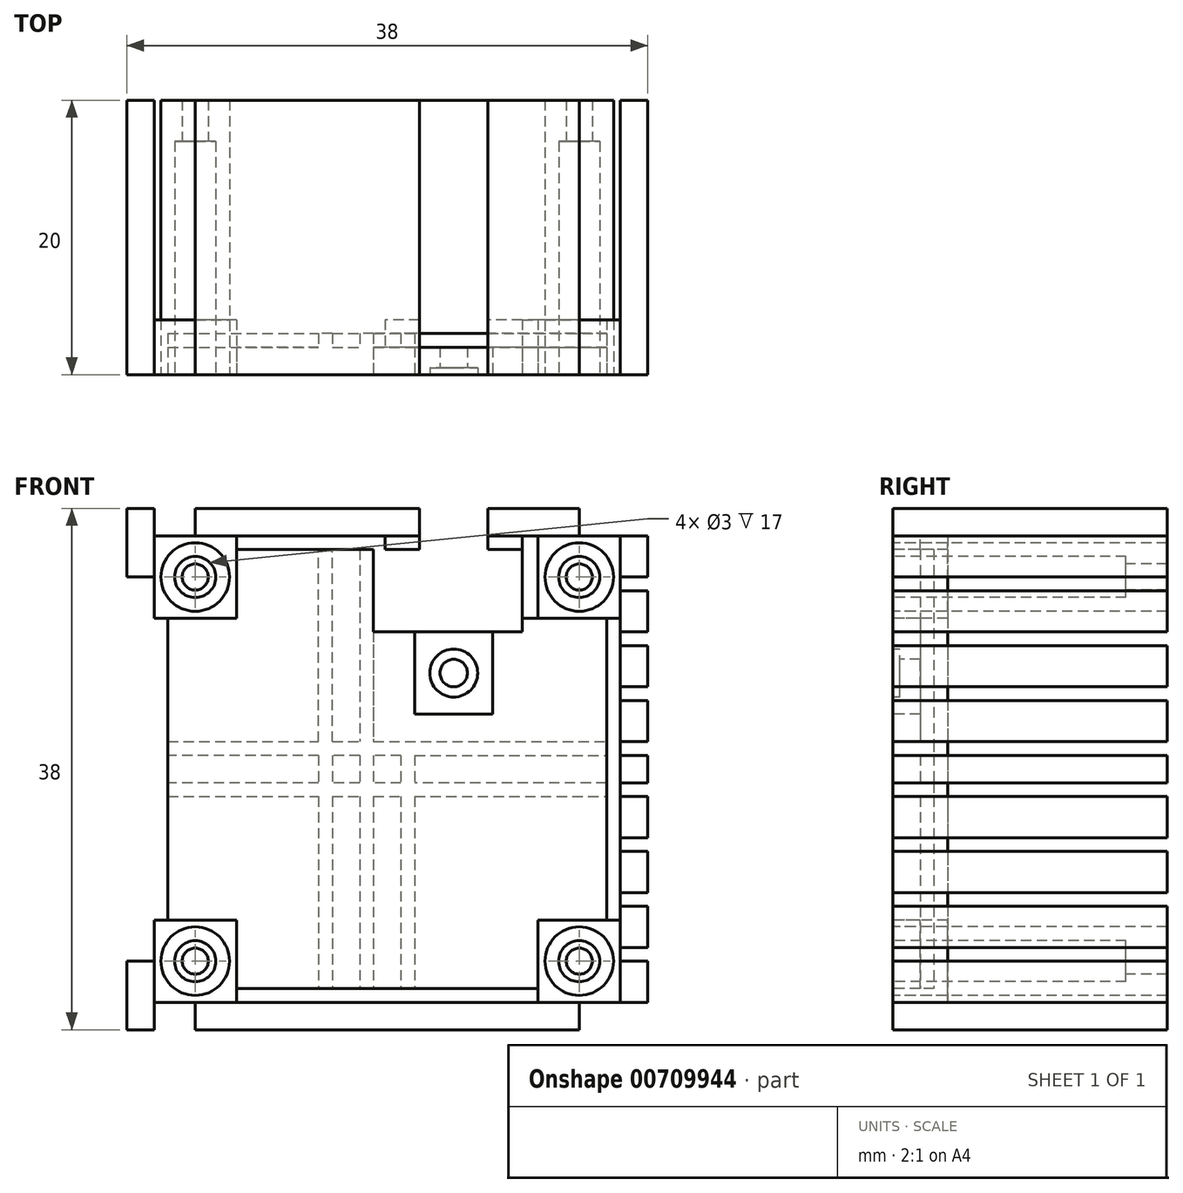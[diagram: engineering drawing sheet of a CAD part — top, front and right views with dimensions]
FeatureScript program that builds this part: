
annotation { "Feature Type Name" : "Feature", "Feature Type Description" : "" }
export const myFeature = defineFeature(function(context is Context, id is Id, definition is map)
    precondition{}
    {
        {
            var Q0;
            Q0=qCreatedBy(makeId("Front.planeOp"),FACE);
            var sketch = newSketch(context, id + "F0", { "sketchPlane" : qUnion([Q0])});
            skLineSegment(sketch, "E0.left", {"start": v(16, 10.17) * mm, "end": v(16, -11) * mm});
            skPoint(sketch, "E0.middle", {"position": v(0, 0) * mm});
            skCircle(sketch, "E1", {"center": v(-14, 14) * mm, "radius": 0.95 * mm});
            skCircle(sketch, "E2", {"center": v(14, -14) * mm, "radius": 0.95 * mm});
            skCircle(sketch, "E3", {"center": v(14, 14) * mm, "radius": 0.95 * mm});
            skCircle(sketch, "E4", {"center": v(-14, -14) * mm, "radius": 0.95 * mm});
            skPoint(sketch, "E5.left.start.orphan", {"position": v(10, -1.28) * mm});
            skPoint(sketch, "E6.trimOffspring.end.orphan", {"position": v(10, 1.28) * mm});
            skPoint(sketch, "E7.trimOffspring.end.orphan", {"position": v(-10, 1.28) * mm});
            skPoint(sketch, "E5.right.start.orphan", {"position": v(-10, -1.28) * mm});
            skLineSegment(sketch, "E8.left", {"start": v(16, 11) * mm, "end": v(16, 10.17) * mm});
            skLineSegment(sketch, "E8.right", {"start": v(9.85, 16) * mm, "end": v(9.85, 10.2) * mm});
            skLineSegment(sketch, "E9.bottom", {"start": v(9.85, 16) * mm, "end": v(-0.15, 16) * mm});
            skLineSegment(sketch, "E9.top", {"start": v(9.85, 10) * mm, "end": v(-0.15, 10) * mm});
            skLineSegment(sketch, "E9.left", {"start": v(9.85, 16) * mm, "end": v(9.85, 10) * mm});
            skLineSegment(sketch, "E9.right", {"start": v(-0.15, 16) * mm, "end": v(-0.15, 10) * mm});
            skLineSegment(sketch, "E10.top", {"start": v(-16, 10) * mm, "end": v(-10, 10) * mm});
            skLineSegment(sketch, "E11.top", {"start": v(-16, 4) * mm, "end": v(-10, 4) * mm});
            skLineSegment(sketch, "E11.left", {"start": v(-16, 10) * mm, "end": v(-16, 4) * mm});
            skLineSegment(sketch, "E11.right", {"start": v(-10, 10) * mm, "end": v(-10, 4) * mm});
            skLineSegment(sketch, "E12.bottom", {"start": v(17, 17) * mm, "end": v(-17, 17) * mm});
            skLineSegment(sketch, "E12.top", {"start": v(17, -17) * mm, "end": v(-17, -17) * mm});
            skLineSegment(sketch, "E12.left", {"start": v(17, 17) * mm, "end": v(17, -17) * mm});
            skLineSegment(sketch, "E12.right", {"start": v(-17, 17) * mm, "end": v(-17, -17) * mm});
            skLineSegment(sketch, "E13.bottom", {"start": v(19, 19) * mm, "end": v(-19, 19) * mm});
            skLineSegment(sketch, "E13.top", {"start": v(19, -19) * mm, "end": v(-19, -19) * mm});
            skLineSegment(sketch, "E13.left", {"start": v(19, 19) * mm, "end": v(19, -19) * mm});
            skLineSegment(sketch, "E13.right", {"start": v(-19, 19) * mm, "end": v(-19, -19) * mm});
            skCircle(sketch, "E14", {"center": v(-14, 14) * mm, "radius": 2.5 * mm});
            skCircle(sketch, "E15", {"center": v(14, 14) * mm, "radius": 2.5 * mm});
            skCircle(sketch, "E16", {"center": v(-14, -14) * mm, "radius": 2.5 * mm});
            skCircle(sketch, "E17", {"center": v(14, -14) * mm, "radius": 2.5 * mm});
            skLineSegment(sketch, "E18.trimOffspring", {"start": v(-16, 11) * mm, "end": v(-16, 10) * mm});
            skLineSegment(sketch, "E19.trimOffspring", {"start": v(-16, 11) * mm, "end": v(-16, -11) * mm});
            skPoint(sketch, "E20.trimOffspring.end.orphan", {"position": v(-16, 16) * mm});
            skLineSegment(sketch, "E21.trimOffspring", {"start": v(11, 16) * mm, "end": v(-11, 16) * mm});
            skLineSegment(sketch, "E22.trimOffspring", {"start": v(11, 16) * mm, "end": v(9.85, 16) * mm});
            skPoint(sketch, "E23.orphan", {"position": v(16, 15.97) * mm});
            skPoint(sketch, "E24.orphan", {"position": v(-16, -15.97) * mm});
            skLineSegment(sketch, "E25.trimOffspring", {"start": v(11, -16) * mm, "end": v(-11, -16) * mm});
            skPoint(sketch, "E26.trimOffspring.end.orphan", {"position": v(16, -16) * mm});
            skPoint(sketch, "E27", {"position": v(8.5, 2) * mm});
            skPoint(sketch, "E28", {"position": v(8.5, -2) * mm});
            skPoint(sketch, "E29", {"position": v(-8.5, 2) * mm});
            skPoint(sketch, "E30", {"position": v(-8.5, -2) * mm});
            skPoint(sketch, "E31.orphan", {"position": v(-8.5, 8.5) * mm});
            skPoint(sketch, "E32.right.start.orphan", {"position": v(-9.5, 9.5) * mm});
            skPoint(sketch, "E33.orphan", {"position": v(-8.5, -8.5) * mm});
            skPoint(sketch, "E32.left.start.orphan", {"position": v(9.5, 9.5) * mm});
            skPoint(sketch, "E34.orphan", {"position": v(8.5, 8.5) * mm});
            skPoint(sketch, "E32.top.end.orphan", {"position": v(-9.5, -9.5) * mm});
            skPoint(sketch, "E35.trimOffspring.end.orphan", {"position": v(9.5, -9.5) * mm});
            skPoint(sketch, "E36.orphan", {"position": v(8.5, -8.5) * mm});
            skLineSegment(sketch, "E37.bottom", {"start": v(2.35, 17) * mm, "end": v(7.35, 17) * mm});
            skLineSegment(sketch, "E37.left", {"start": v(2.35, 17) * mm, "end": v(2.35, 11) * mm});
            skLineSegment(sketch, "E37.right", {"start": v(7.35, 17) * mm, "end": v(7.35, 11) * mm});
            skPoint(sketch, "E37.middle", {"position": v(4.85, 13) * mm});
            skLineSegment(sketch, "E38", {"start": v(2.35, 17) * mm, "end": v(2.35, 19) * mm});
            skLineSegment(sketch, "E39", {"start": v(7.35, 17) * mm, "end": v(7.35, 19) * mm});
            skPoint(sketch, "E40.center.orphan", {"position": v(-10, 0) * mm});
            skPoint(sketch, "E41.center.orphan", {"position": v(10, 0) * mm});
            skPoint(sketch, "E42", {"position": v(7.35, 16) * mm});
            skLineSegment(sketch, "E43.bottom", {"start": v(2.35, 16) * mm, "end": v(7.35, 16) * mm});
            skLineSegment(sketch, "E43.top", {"start": v(2.35, 11) * mm, "end": v(7.35, 11) * mm});
            skLineSegment(sketch, "E43.left", {"start": v(2.35, 16) * mm, "end": v(2.35, 11) * mm});
            skLineSegment(sketch, "E43.right", {"start": v(7.35, 16) * mm, "end": v(7.35, 11) * mm});
            skPoint(sketch, "E44", {"position": v(2.35, 10) * mm});
            skPoint(sketch, "E45", {"position": v(7.35, 10) * mm});
            skPoint(sketch, "E37.top.start.orphan", {"position": v(2.35, 9) * mm});
            skPoint(sketch, "E46.orphan", {"position": v(7.35, 9) * mm});
            skPoint(sketch, "E47", {"position": v(2.35, 11) * mm});
            skPoint(sketch, "E48", {"position": v(7.35, 11) * mm});
            skLineSegment(sketch, "E49.bottom", {"start": v(-19, 19) * mm, "end": v(-17, 19) * mm});
            skLineSegment(sketch, "E49.top", {"start": v(-19, 17) * mm, "end": v(-17, 17) * mm});
            skLineSegment(sketch, "E49.left", {"start": v(-19, 19) * mm, "end": v(-19, 17) * mm});
            skLineSegment(sketch, "E49.right", {"start": v(-17, 19) * mm, "end": v(-17, 17) * mm});
            skLineSegment(sketch, "E50.bottom", {"start": v(19, 19) * mm, "end": v(17, 19) * mm});
            skLineSegment(sketch, "E50.top", {"start": v(19, 17) * mm, "end": v(17, 17) * mm});
            skLineSegment(sketch, "E50.left", {"start": v(19, 19) * mm, "end": v(19, 17) * mm});
            skLineSegment(sketch, "E50.right", {"start": v(17, 19) * mm, "end": v(17, 17) * mm});
            skLineSegment(sketch, "E51.bottom", {"start": v(17, -17) * mm, "end": v(19, -17) * mm});
            skLineSegment(sketch, "E51.top", {"start": v(17, -19) * mm, "end": v(19, -19) * mm});
            skLineSegment(sketch, "E51.left", {"start": v(17, -17) * mm, "end": v(17, -19) * mm});
            skLineSegment(sketch, "E51.right", {"start": v(19, -17) * mm, "end": v(19, -19) * mm});
            skLineSegment(sketch, "E52.bottom", {"start": v(-19, -19) * mm, "end": v(-17, -19) * mm});
            skLineSegment(sketch, "E52.top", {"start": v(-19, -17) * mm, "end": v(-17, -17) * mm});
            skLineSegment(sketch, "E52.left", {"start": v(-19, -19) * mm, "end": v(-19, -17) * mm});
            skLineSegment(sketch, "E52.right", {"start": v(-17, -19) * mm, "end": v(-17, -17) * mm});
            skLineSegment(sketch, "E53.bottom", {"start": v(-17, -17) * mm, "end": v(-19, -17) * mm});
            skLineSegment(sketch, "E53.top", {"start": v(-17, -14) * mm, "end": v(-19, -14) * mm});
            skLineSegment(sketch, "E53.left", {"start": v(-17, -17) * mm, "end": v(-17, -14) * mm});
            skLineSegment(sketch, "E53.right", {"start": v(-19, -17) * mm, "end": v(-19, -14) * mm});
            skLineSegment(sketch, "E54.top", {"start": v(17, -14) * mm, "end": v(19, -14) * mm});
            skLineSegment(sketch, "E54.left", {"start": v(17, -17) * mm, "end": v(17, -14) * mm});
            skLineSegment(sketch, "E54.right", {"start": v(19, -17) * mm, "end": v(19, -14) * mm});
            skLineSegment(sketch, "E55.bottom", {"start": v(-17, -17) * mm, "end": v(-14, -17) * mm});
            skLineSegment(sketch, "E55.top", {"start": v(-17, -19) * mm, "end": v(-14, -19) * mm});
            skLineSegment(sketch, "E55.left", {"start": v(-17, -17) * mm, "end": v(-17, -19) * mm});
            skLineSegment(sketch, "E55.right", {"start": v(-14, -17) * mm, "end": v(-14, -19) * mm});
            skLineSegment(sketch, "E56.bottom", {"start": v(17, -19) * mm, "end": v(14, -19) * mm});
            skLineSegment(sketch, "E56.top", {"start": v(17, -17) * mm, "end": v(14, -17) * mm});
            skLineSegment(sketch, "E56.left", {"start": v(17, -19) * mm, "end": v(17, -17) * mm});
            skLineSegment(sketch, "E56.right", {"start": v(14, -19) * mm, "end": v(14, -17) * mm});
            skLineSegment(sketch, "E57.top", {"start": v(-19, 14) * mm, "end": v(-17, 14) * mm});
            skLineSegment(sketch, "E57.left", {"start": v(-19, 17) * mm, "end": v(-19, 14) * mm});
            skLineSegment(sketch, "E57.right", {"start": v(-17, 17) * mm, "end": v(-17, 14) * mm});
            skLineSegment(sketch, "E58.bottom", {"start": v(-17, 19) * mm, "end": v(-14, 19) * mm});
            skLineSegment(sketch, "E58.top", {"start": v(-17, 17) * mm, "end": v(-14, 17) * mm});
            skLineSegment(sketch, "E58.right", {"start": v(-14, 19) * mm, "end": v(-14, 17) * mm});
            skLineSegment(sketch, "E59.bottom", {"start": v(17, 19) * mm, "end": v(14, 19) * mm});
            skLineSegment(sketch, "E59.top", {"start": v(17, 17) * mm, "end": v(14, 17) * mm});
            skLineSegment(sketch, "E59.right", {"start": v(14, 19) * mm, "end": v(14, 17) * mm});
            skLineSegment(sketch, "E60.top", {"start": v(19, 14) * mm, "end": v(17, 14) * mm});
            skLineSegment(sketch, "E60.left", {"start": v(19, 17) * mm, "end": v(19, 14) * mm});
            skLineSegment(sketch, "E60.right", {"start": v(17, 17) * mm, "end": v(17, 14) * mm});
            skLineSegment(sketch, "E61.bottom", {"start": v(17, 14) * mm, "end": v(19, 14) * mm});
            skLineSegment(sketch, "E61.top", {"start": v(17, 13) * mm, "end": v(19, 13) * mm});
            skLineSegment(sketch, "E61.left", {"start": v(17, 14) * mm, "end": v(17, 13) * mm});
            skLineSegment(sketch, "E61.right", {"start": v(19, 14) * mm, "end": v(19, 13) * mm});
            skPoint(sketch, "E62", {"position": v(19, 14) * mm});
            skPoint(sketch, "E63", {"position": v(19, 13) * mm});
            skLineSegment(sketch, "E64.top", {"start": v(17, 10) * mm, "end": v(19, 10) * mm});
            skLineSegment(sketch, "E64.left", {"start": v(17, 13) * mm, "end": v(17, 10) * mm});
            skLineSegment(sketch, "E64.right", {"start": v(19, 13) * mm, "end": v(19, 10) * mm});
            skLineSegment(sketch, "E65.top", {"start": v(17, 9) * mm, "end": v(19, 9) * mm});
            skLineSegment(sketch, "E65.left", {"start": v(17, 10) * mm, "end": v(17, 9) * mm});
            skLineSegment(sketch, "E65.right", {"start": v(19, 10) * mm, "end": v(19, 9) * mm});
            skLineSegment(sketch, "E66.top", {"start": v(17, 6) * mm, "end": v(19, 6) * mm});
            skLineSegment(sketch, "E66.left", {"start": v(17, 9) * mm, "end": v(17, 6) * mm});
            skLineSegment(sketch, "E66.right", {"start": v(19, 9) * mm, "end": v(19, 6) * mm});
            skLineSegment(sketch, "E67.top", {"start": v(17, 5) * mm, "end": v(19, 5) * mm});
            skLineSegment(sketch, "E67.left", {"start": v(17, 6) * mm, "end": v(17, 5) * mm});
            skLineSegment(sketch, "E67.right", {"start": v(19, 6) * mm, "end": v(19, 5) * mm});
            skLineSegment(sketch, "E68.top", {"start": v(17, 2) * mm, "end": v(19, 2) * mm});
            skLineSegment(sketch, "E68.left", {"start": v(17, 5) * mm, "end": v(17, 2) * mm});
            skLineSegment(sketch, "E68.right", {"start": v(19, 5) * mm, "end": v(19, 2) * mm});
            skLineSegment(sketch, "E69.left", {"start": v(17, 2) * mm, "end": v(17, 0) * mm});
            skLineSegment(sketch, "E69.right", {"start": v(19, 2) * mm, "end": v(19, 0) * mm});
            skLineSegment(sketch, "E70.top", {"start": v(17, -2) * mm, "end": v(19, -2) * mm});
            skLineSegment(sketch, "E70.left", {"start": v(17, 0) * mm, "end": v(17, -2) * mm});
            skLineSegment(sketch, "E70.right", {"start": v(19, 0) * mm, "end": v(19, -2) * mm});
            skLineSegment(sketch, "E71.top", {"start": v(17, -5) * mm, "end": v(19, -5) * mm});
            skLineSegment(sketch, "E71.left", {"start": v(17, -2) * mm, "end": v(17, -5) * mm});
            skLineSegment(sketch, "E71.right", {"start": v(19, -2) * mm, "end": v(19, -5) * mm});
            skLineSegment(sketch, "E72.top", {"start": v(17, -6) * mm, "end": v(19, -6) * mm});
            skLineSegment(sketch, "E72.left", {"start": v(17, -5) * mm, "end": v(17, -6) * mm});
            skLineSegment(sketch, "E72.right", {"start": v(19, -5) * mm, "end": v(19, -6) * mm});
            skLineSegment(sketch, "E73.top", {"start": v(17, -9) * mm, "end": v(19, -9) * mm});
            skLineSegment(sketch, "E73.left", {"start": v(17, -6) * mm, "end": v(17, -9) * mm});
            skLineSegment(sketch, "E73.right", {"start": v(19, -6) * mm, "end": v(19, -9) * mm});
            skLineSegment(sketch, "E74.top", {"start": v(17, -10) * mm, "end": v(19, -10) * mm});
            skLineSegment(sketch, "E74.left", {"start": v(17, -9) * mm, "end": v(17, -10) * mm});
            skLineSegment(sketch, "E74.right", {"start": v(19, -9) * mm, "end": v(19, -10) * mm});
            skLineSegment(sketch, "E75.top", {"start": v(17, -13) * mm, "end": v(19, -13) * mm});
            skLineSegment(sketch, "E75.left", {"start": v(17, -10) * mm, "end": v(17, -13) * mm});
            skLineSegment(sketch, "E75.right", {"start": v(19, -10) * mm, "end": v(19, -13) * mm});
            skLineSegment(sketch, "E76", {"start": v(17, -1) * mm, "end": v(19, -1) * mm});
            skLineSegment(sketch, "E77", {"start": v(17, 1) * mm, "end": v(19, 1) * mm});
            skLineSegment(sketch, "E78.bottom", {"start": v(1, 16) * mm, "end": v(-1, 16) * mm});
            skLineSegment(sketch, "E78.top", {"start": v(1, -16) * mm, "end": v(-1, -16) * mm});
            skLineSegment(sketch, "E78.right", {"start": v(-1, 16) * mm, "end": v(-1, 2) * mm});
            skLineSegment(sketch, "E79.top", {"start": v(16, -1) * mm, "end": v(2, -1) * mm});
            skLineSegment(sketch, "E79.left", {"start": v(17, 1) * mm, "end": v(17, -1) * mm});
            skLineSegment(sketch, "E79.right", {"start": v(-17, 1) * mm, "end": v(-17, -1) * mm});
            skLineSegment(sketch, "E80.bottom", {"start": v(-16, 2) * mm, "end": v(-5, 2) * mm});
            skLineSegment(sketch, "E80.top", {"start": v(-16, -2) * mm, "end": v(-5, -2) * mm});
            skLineSegment(sketch, "E80.left", {"start": v(-17, 2) * mm, "end": v(-17, -2) * mm});
            skLineSegment(sketch, "E80.right", {"start": v(17, 2) * mm, "end": v(17, -2) * mm});
            skLineSegment(sketch, "E81.bottom", {"start": v(-2, 16) * mm, "end": v(2, 16) * mm});
            skLineSegment(sketch, "E81.top", {"start": v(-2, -16) * mm, "end": v(2, -16) * mm});
            skLineSegment(sketch, "E81.left", {"start": v(-2, 16) * mm, "end": v(-2, 2) * mm});
            skLineSegment(sketch, "E81.right", {"start": v(2, 10) * mm, "end": v(2, 4) * mm});
            skLineSegment(sketch, "E82.trimOffspring", {"start": v(-1, 2) * mm, "end": v(1, 2) * mm});
            skLineSegment(sketch, "E83.trimOffspring", {"start": v(-2, 1) * mm, "end": v(-4, 1) * mm});
            skLineSegment(sketch, "E84.trimOffspring", {"start": v(2, 2) * mm, "end": v(16, 2) * mm});
            skLineSegment(sketch, "E85.trimOffspring", {"start": v(1, 1) * mm, "end": v(1, -1) * mm});
            skLineSegment(sketch, "E86.trimOffspring", {"start": v(1, 1) * mm, "end": v(-1, 1) * mm});
            skLineSegment(sketch, "E87.trimOffspring", {"start": v(1, -1) * mm, "end": v(-1, -1) * mm});
            skLineSegment(sketch, "E88.trimOffspring", {"start": v(2, -2) * mm, "end": v(16, -2) * mm});
            skPoint(sketch, "E89", {"position": v(2, -1) * mm});
            skPoint(sketch, "E90", {"position": v(2, -2) * mm});
            skPoint(sketch, "E91", {"position": v(1, -2) * mm});
            skPoint(sketch, "E92", {"position": v(1, -1) * mm});
            skPoint(sketch, "E93", {"position": v(-1, -1) * mm});
            skPoint(sketch, "E94", {"position": v(-1, -2) * mm});
            skPoint(sketch, "E95", {"position": v(-2, -2) * mm});
            skPoint(sketch, "E96", {"position": v(-2, -1) * mm});
            skPoint(sketch, "E97", {"position": v(-2, 1) * mm});
            skPoint(sketch, "E98", {"position": v(-1, 1) * mm});
            skLineSegment(sketch, "E99.trimOffspring", {"start": v(-2, -2) * mm, "end": v(-2, -16) * mm});
            skLineSegment(sketch, "E100.trimOffspring", {"start": v(-1, -2) * mm, "end": v(-1, -16) * mm});
            skLineSegment(sketch, "E101.trimOffspring", {"start": v(-1, -2) * mm, "end": v(1, -2) * mm});
            skLineSegment(sketch, "E102.trimOffspring", {"start": v(-2, 1) * mm, "end": v(-2, -1) * mm});
            skLineSegment(sketch, "E103.trimOffspring", {"start": v(-2, -1) * mm, "end": v(-4, -1) * mm});
            skLineSegment(sketch, "E104.trimOffspring", {"start": v(-1, 1) * mm, "end": v(-1, -1) * mm});
            skLineSegment(sketch, "E105.trimOffspring", {"start": v(2, 1) * mm, "end": v(2, -1) * mm});
            skLineSegment(sketch, "E106.trimOffspring", {"start": v(2, -2) * mm, "end": v(2, -16) * mm});
            skLineSegment(sketch, "E107.trimOffspring", {"start": v(1, -2) * mm, "end": v(1, -16) * mm});
            skLineSegment(sketch, "E108", {"start": v(2, 1) * mm, "end": v(16, 1) * mm});
            skCircle(sketch, "E109", {"center": v(14, 14) * mm, "radius": 1.5 * mm});
            skCircle(sketch, "E110", {"center": v(-14, 14) * mm, "radius": 1.5 * mm});
            skCircle(sketch, "E111", {"center": v(14, -14) * mm, "radius": 1.5 * mm});
            skCircle(sketch, "E112", {"center": v(-14, -14) * mm, "radius": 1.5 * mm});
            skLineSegment(sketch, "E113.bottom", {"start": v(17, 17) * mm, "end": v(11, 17) * mm});
            skLineSegment(sketch, "E113.top", {"start": v(17, 11) * mm, "end": v(11, 11) * mm});
            skLineSegment(sketch, "E113.left", {"start": v(17, 17) * mm, "end": v(17, 11) * mm});
            skLineSegment(sketch, "E113.right", {"start": v(11, 17) * mm, "end": v(11, 11) * mm});
            skLineSegment(sketch, "E114.bottom", {"start": v(-17, 17) * mm, "end": v(-11, 17) * mm});
            skLineSegment(sketch, "E114.top", {"start": v(-17, 11) * mm, "end": v(-11, 11) * mm});
            skLineSegment(sketch, "E114.left", {"start": v(-17, 17) * mm, "end": v(-17, 11) * mm});
            skLineSegment(sketch, "E114.right", {"start": v(-11, 17) * mm, "end": v(-11, 11) * mm});
            skLineSegment(sketch, "E115.bottom", {"start": v(-17, -17) * mm, "end": v(-11, -17) * mm});
            skLineSegment(sketch, "E115.top", {"start": v(-17, -11) * mm, "end": v(-11, -11) * mm});
            skLineSegment(sketch, "E115.left", {"start": v(-17, -17) * mm, "end": v(-17, -11) * mm});
            skLineSegment(sketch, "E115.right", {"start": v(-11, -17) * mm, "end": v(-11, -11) * mm});
            skLineSegment(sketch, "E116.bottom", {"start": v(17, -17) * mm, "end": v(11, -17) * mm});
            skLineSegment(sketch, "E116.top", {"start": v(17, -11) * mm, "end": v(11, -11) * mm});
            skLineSegment(sketch, "E116.left", {"start": v(17, -17) * mm, "end": v(17, -11) * mm});
            skLineSegment(sketch, "E116.right", {"start": v(11, -17) * mm, "end": v(11, -11) * mm});
            skLineSegment(sketch, "E117.bottom", {"start": v(9.85, 16) * mm, "end": v(11, 16) * mm});
            skLineSegment(sketch, "E117.top", {"start": v(9.85, 11) * mm, "end": v(11, 11) * mm});
            skLineSegment(sketch, "E117.left", {"start": v(9.85, 16) * mm, "end": v(9.85, 11) * mm});
            skLineSegment(sketch, "E117.right", {"start": v(11, 16) * mm, "end": v(11, 11) * mm});
            skLineSegment(sketch, "E118.bottom", {"start": v(-0.15, 16) * mm, "end": v(-1, 16) * mm});
            skLineSegment(sketch, "E118.top", {"start": v(-0.15, 10) * mm, "end": v(-1, 10) * mm});
            skLineSegment(sketch, "E118.right", {"start": v(-1, 16) * mm, "end": v(-1, 10) * mm});
            skPoint(sketch, "E119", {"position": v(4.85, 10) * mm});
            skArc(sketch, "E120", {"start": v(7.7, 7.94) * mm, "mid": v(4.85, 10) * mm, "end": v(2, 7.94) * mm});
            skCircle(sketch, "E121", {"center": v(4.85, 7) * mm, "radius": 1 * mm});
            skCircle(sketch, "E122", {"center": v(4.85, 7) * mm, "radius": 1.75 * mm});
            skLineSegment(sketch, "E123.bottom", {"start": v(2, 10) * mm, "end": v(7.7, 10) * mm});
            skLineSegment(sketch, "E123.top", {"start": v(2, 4) * mm, "end": v(7.7, 4) * mm});
            skLineSegment(sketch, "E123.right", {"start": v(7.7, 10) * mm, "end": v(7.7, 4) * mm});
            skArc(sketch, "E124.trimOffspring", {"start": v(2, 6.06) * mm, "mid": v(4.85, 4) * mm, "end": v(7.7, 6.06) * mm});
            skLineSegment(sketch, "E125", {"start": v(-4, 2) * mm, "end": v(-4, 16) * mm});
            skLineSegment(sketch, "E126", {"start": v(-5, 2) * mm, "end": v(-5, 16) * mm});
            skLineSegment(sketch, "E127", {"start": v(-4, 1) * mm, "end": v(-4, -1) * mm});
            skLineSegment(sketch, "E128", {"start": v(-5, 1) * mm, "end": v(-5, -1) * mm});
            skLineSegment(sketch, "E129", {"start": v(-5, -2) * mm, "end": v(-5, -16) * mm});
            skLineSegment(sketch, "E130", {"start": v(-4, -2) * mm, "end": v(-4, -16) * mm});
            skLineSegment(sketch, "E131.trimOffspring", {"start": v(-5, -1) * mm, "end": v(-16, -1) * mm});
            skLineSegment(sketch, "E132.trimOffspring", {"start": v(-4, -2) * mm, "end": v(-2, -2) * mm});
            skLineSegment(sketch, "E133.trimOffspring", {"start": v(-4, 2) * mm, "end": v(-2, 2) * mm});
            skLineSegment(sketch, "E134.trimOffspring", {"start": v(-5, 1) * mm, "end": v(-16, 1) * mm});
            skLineSegment(sketch, "E135", {"start": v(2, 2) * mm, "end": v(1, 2) * mm});
            skLineSegment(sketch, "E136", {"start": v(9.85, 16) * mm, "end": v(9.85, 17) * mm});
            skLineSegment(sketch, "E137", {"start": v(-0.15, 16) * mm, "end": v(-0.15, 17) * mm});
            skSolve(sketch);
        }
        {
            var Q0;
            {var subQ20=sQuery(id+"F0.wireOp",EDGE,"E78.right");Q0=makeQuery(id+"F0.imprint","IMPRINT",FACE,{"disambiguationData":[TD([[makeQuery(id+"F0.imprint","IMPRINT",EDGE,{"derivedFrom":subQ20}),-1.0]])]});}
            var Q1;
            {var subQ0=sQuery(id+"F0.wireOp",EDGE,"E78.left");Q1=makeQuery(id+"F0.imprint","IMPRINT",FACE,{"disambiguationData":[TD([[makeQuery(id+"F0.imprint","IMPRINT",EDGE,{"derivedFrom":subQ0}),1.0]])]});}
            extrude(context, id + "F1", {"entities" : qUnion([Q0, Q1]), "oppositeDirection" : true, "depth" : 3 * mm, "offsetDistance" : 25 * mm});
        }
        {
            var Q0;
            {var subQ1=sQuery(id+"F0.wireOp",EDGE,"E8.left");Q0=makeQuery(id+"F0.imprint","IMPRINT",FACE,{"disambiguationData":[TD([[makeQuery(id+"F0.imprint","IMPRINT",EDGE,{"derivedFrom":subQ1}),-1.0]])]});}
            var Q1;
            {var subQ0=sQuery(id+"F0.wireOp",EDGE,"E81.left");Q1=makeQuery(id+"F0.imprint","IMPRINT",FACE,{"disambiguationData":[TD([[makeQuery(id+"F0.imprint","IMPRINT",EDGE,{"derivedFrom":subQ0}),-1.0]])]});}
            var Q2;
            {var subQ0=sQuery(id+"F0.wireOp",EDGE,"E88.trimOffspring");Q2=makeQuery(id+"F0.imprint","IMPRINT",FACE,{"disambiguationData":[TD([[makeQuery(id+"F0.imprint","IMPRINT",EDGE,{"derivedFrom":subQ0}),-1.0]])]});}
            var Q3;
            {var subQ0=sQuery(id+"F0.wireOp",EDGE,"E79.top");Q3=makeQuery(id+"F0.imprint","IMPRINT",FACE,{"disambiguationData":[TD([[makeQuery(id+"F0.imprint","IMPRINT",EDGE,{"derivedFrom":subQ0}),-1.0]])]});}
            var Q4;
            Q4=makeQuery(id+"F0.imprint","IMPRINT",FACE,{"disambiguationData":[TD([[makeQuery(id+"F0.imprint","IMPRINT",EDGE,{"derivedFrom":sQuery(id+"F0.wireOp",EDGE,"E128")}),-1.0]])]});
            var Q5;
            {var subQ5=sQuery(id+"F0.wireOp",EDGE,"E80.top");Q5=makeQuery(id+"F0.imprint","IMPRINT",FACE,{"disambiguationData":[TD([[makeQuery(id+"F0.imprint","IMPRINT",EDGE,{"derivedFrom":subQ5}),-1.0]])]});}
            var Q6;
            {var subQ0=sQuery(id+"F0.wireOp",EDGE,"E99.trimOffspring");Q6=makeQuery(id+"F0.imprint","IMPRINT",FACE,{"disambiguationData":[TD([[makeQuery(id+"F0.imprint","IMPRINT",EDGE,{"derivedFrom":subQ0}),-1.0]])]});}
            var Q7;
            {var subQ0=sQuery(id+"F0.wireOp",EDGE,"E100.trimOffspring");Q7=makeQuery(id+"F0.imprint","IMPRINT",FACE,{"disambiguationData":[TD([[makeQuery(id+"F0.imprint","IMPRINT",EDGE,{"derivedFrom":subQ0}),1.0]])]});}
            var Q8;
            {var subQ1=sQuery(id+"F0.wireOp",EDGE,"E10.top");Q8=makeQuery(id+"F0.imprint","IMPRINT",FACE,{"disambiguationData":[TD([[makeQuery(id+"F0.imprint","IMPRINT",EDGE,{"derivedFrom":subQ1}),1.0]])]});}
            var Q9;
            Q9=makeQuery(id+"F0.imprint","IMPRINT",FACE,{"disambiguationData":[TD([[makeQuery(id+"F0.imprint","IMPRINT",EDGE,{"derivedFrom":sQuery(id+"F0.wireOp",EDGE,"E83.trimOffspring")}),1.0]])]});
            var Q10;
            Q10=makeQuery(id+"F0.imprint","IMPRINT",FACE,{"disambiguationData":[TD([[makeQuery(id+"F0.imprint","IMPRINT",EDGE,{"derivedFrom":sQuery(id+"F0.wireOp",EDGE,"E85.trimOffspring")}),-1.0]])]});
            extrude(context, id + "F2", {"entities" : qUnion([Q0, Q1, Q2, Q3, Q4, Q5, Q6, Q7, Q8, Q9, Q10]), "operationType" : NewBodyOperationType.ADD, "oppositeDirection" : true, "depth" : 2 * mm, "offsetDistance" : 25 * mm});
        }
        {
            var Q0;
            Q0=makeQuery(id+"F0.imprint","IMPRINT",FACE,{"disambiguationData":[TD([[makeQuery(id+"F0.imprint","IMPRINT",EDGE,{"derivedFrom":sQuery(id+"F0.wireOp",EDGE,"E15")}),-1.0]])]});
            var Q1;
            Q1=makeQuery(id+"F0.imprint","IMPRINT",FACE,{"disambiguationData":[TD([[makeQuery(id+"F0.imprint","IMPRINT",EDGE,{"derivedFrom":sQuery(id+"F0.wireOp",EDGE,"E14")}),-1.0]])]});
            var Q2;
            Q2=makeQuery(id+"F0.imprint","IMPRINT",FACE,{"disambiguationData":[TD([[makeQuery(id+"F0.imprint","IMPRINT",EDGE,{"derivedFrom":sQuery(id+"F0.wireOp",EDGE,"E16")}),-1.0]])]});
            var Q3;
            Q3=makeQuery(id+"F0.imprint","IMPRINT",FACE,{"disambiguationData":[TD([[makeQuery(id+"F0.imprint","IMPRINT",EDGE,{"derivedFrom":sQuery(id+"F0.wireOp",EDGE,"E17")}),-1.0]])]});
            extrude(context, id + "F3", {"entities" : qUnion([Q0, Q1, Q2, Q3]), "oppositeDirection" : true, "depth" : 4 * mm, "offsetDistance" : 25 * mm});
        }
        {
            var Q0;
            Q0=makeQuery(id+"F0.imprint","IMPRINT",FACE,{"disambiguationData":[TD([[makeQuery(id+"F0.imprint","IMPRINT",EDGE,{"derivedFrom":sQuery(id+"F0.wireOp",EDGE,"E15")}),1.0]])]});
            var Q1;
            Q1=makeQuery(id+"F0.imprint","IMPRINT",FACE,{"disambiguationData":[TD([[makeQuery(id+"F0.imprint","IMPRINT",EDGE,{"derivedFrom":sQuery(id+"F0.wireOp",EDGE,"E3")}),-1.0]])]});
            var Q2;
            Q2=makeQuery(id+"F0.imprint","IMPRINT",FACE,{"disambiguationData":[TD([[makeQuery(id+"F0.imprint","IMPRINT",EDGE,{"derivedFrom":sQuery(id+"F0.wireOp",EDGE,"E14")}),1.0]])]});
            var Q3;
            Q3=makeQuery(id+"F0.imprint","IMPRINT",FACE,{"disambiguationData":[TD([[makeQuery(id+"F0.imprint","IMPRINT",EDGE,{"derivedFrom":sQuery(id+"F0.wireOp",EDGE,"E1")}),-1.0]])]});
            var Q4;
            Q4=makeQuery(id+"F0.imprint","IMPRINT",FACE,{"disambiguationData":[TD([[makeQuery(id+"F0.imprint","IMPRINT",EDGE,{"derivedFrom":sQuery(id+"F0.wireOp",EDGE,"E16")}),1.0]])]});
            var Q5;
            Q5=makeQuery(id+"F0.imprint","IMPRINT",FACE,{"disambiguationData":[TD([[makeQuery(id+"F0.imprint","IMPRINT",EDGE,{"derivedFrom":sQuery(id+"F0.wireOp",EDGE,"E4")}),-1.0]])]});
            var Q6;
            Q6=makeQuery(id+"F0.imprint","IMPRINT",FACE,{"disambiguationData":[TD([[makeQuery(id+"F0.imprint","IMPRINT",EDGE,{"derivedFrom":sQuery(id+"F0.wireOp",EDGE,"E17")}),1.0]])]});
            var Q7;
            Q7=makeQuery(id+"F0.imprint","IMPRINT",FACE,{"disambiguationData":[TD([[makeQuery(id+"F0.imprint","IMPRINT",EDGE,{"derivedFrom":sQuery(id+"F0.wireOp",EDGE,"E2")}),-1.0]])]});
            extrude(context, id + "F4", {"entities" : qUnion([Q0, Q1, Q2, Q3, Q4, Q5, Q6, Q7]), "oppositeDirection" : true, "depth" : 20 * mm, "offsetDistance" : 25 * mm});
        }
        {
            var Q0;
            Q0=makeQuery(id+"F0.imprint","IMPRINT",FACE,{"disambiguationData":[TD([[makeQuery(id+"F0.imprint","IMPRINT",EDGE,{"derivedFrom":sQuery(id+"F0.wireOp",EDGE,"E1")}),-1.0]])]});
            extrude(context, id + "F5", {"entities" : qUnion([Q0]), "operationType" : NewBodyOperationType.REMOVE, "oppositeDirection" : true, "depth" : 17 * mm, "offsetDistance" : 25 * mm});
        }
        {
            var Q0;
            Q0=makeQuery(id+"F0.imprint","IMPRINT",FACE,{"disambiguationData":[TD([[makeQuery(id+"F0.imprint","IMPRINT",EDGE,{"derivedFrom":sQuery(id+"F0.wireOp",EDGE,"E3")}),-1.0]])]});
            extrude(context, id + "F6", {"entities" : qUnion([Q0]), "operationType" : NewBodyOperationType.REMOVE, "oppositeDirection" : true, "depth" : 17 * mm, "offsetDistance" : 25 * mm});
        }
        {
            var Q0;
            Q0=makeQuery(id+"F0.imprint","IMPRINT",FACE,{"disambiguationData":[TD([[makeQuery(id+"F0.imprint","IMPRINT",EDGE,{"derivedFrom":sQuery(id+"F0.wireOp",EDGE,"E4")}),-1.0]])]});
            extrude(context, id + "F7", {"entities" : qUnion([Q0]), "operationType" : NewBodyOperationType.REMOVE, "oppositeDirection" : true, "depth" : 17 * mm, "offsetDistance" : 25 * mm});
        }
        {
            var Q0;
            Q0=makeQuery(id+"F0.imprint","IMPRINT",FACE,{"disambiguationData":[TD([[makeQuery(id+"F0.imprint","IMPRINT",EDGE,{"derivedFrom":sQuery(id+"F0.wireOp",EDGE,"E2")}),-1.0]])]});
            extrude(context, id + "F8", {"entities" : qUnion([Q0]), "operationType" : NewBodyOperationType.REMOVE, "oppositeDirection" : true, "depth" : 17 * mm, "offsetDistance" : 25 * mm});
        }
        {
            var Q0;
            {var subQ0=sQuery(id+"F0.wireOp",EDGE,"E10.top");Q0=makeQuery(id+"F0.imprint","IMPRINT",FACE,{"disambiguationData":[TD([[makeQuery(id+"F0.imprint","IMPRINT",EDGE,{"derivedFrom":subQ0}),-1.0]])]});}
            extrude(context, id + "F9", {"entities" : qUnion([Q0]), "operationType" : NewBodyOperationType.ADD, "oppositeDirection" : true, "depth" : 2 * mm, "offsetDistance" : 25 * mm});
        }
        {
            var Q0;
            Q0=makeQuery(id+"F0.imprint","IMPRINT",FACE,{"disambiguationData":[TD([[makeQuery(id+"F0.imprint","IMPRINT",EDGE,{"derivedFrom":sQuery(id+"F0.wireOp",EDGE,"E50.bottom")}),1.0]])]});
            var Q1;
            {var subQ0=sQuery(id+"F0.wireOp",EDGE,"E50.top");Q1=makeQuery(id+"F0.imprint","IMPRINT",FACE,{"disambiguationData":[TD([[makeQuery(id+"F0.imprint","IMPRINT",EDGE,{"derivedFrom":subQ0}),1.0]])]});}
            var Q2;
            Q2=makeQuery(id+"F0.imprint","IMPRINT",FACE,{"disambiguationData":[TD([[makeQuery(id+"F0.imprint","IMPRINT",EDGE,{"derivedFrom":sQuery(id+"F0.wireOp",EDGE,"E59.bottom")}),1.0]])]});
            var Q3;
            {var subQ0=sQuery(id+"F0.wireOp",EDGE,"E39");Q3=makeQuery(id+"F0.imprint","IMPRINT",FACE,{"disambiguationData":[TD([[makeQuery(id+"F0.imprint","IMPRINT",EDGE,{"derivedFrom":subQ0}),-1.0]])]});}
            var Q4;
            Q4=makeQuery(id+"F0.imprint","IMPRINT",FACE,{"disambiguationData":[TD([[makeQuery(id+"F0.imprint","IMPRINT",EDGE,{"derivedFrom":sQuery(id+"F0.wireOp",EDGE,"E37.bottom")}),1.0]])]});
            var Q5;
            {var subQ0=sQuery(id+"F0.wireOp",EDGE,"E38");Q5=makeQuery(id+"F0.imprint","IMPRINT",FACE,{"disambiguationData":[TD([[makeQuery(id+"F0.imprint","IMPRINT",EDGE,{"derivedFrom":subQ0}),1.0]])]});}
            var Q6;
            Q6=makeQuery(id+"F0.imprint","IMPRINT",FACE,{"disambiguationData":[TD([[makeQuery(id+"F0.imprint","IMPRINT",EDGE,{"derivedFrom":sQuery(id+"F0.wireOp",EDGE,"E58.bottom")}),-1.0]])]});
            var Q7;
            Q7=makeQuery(id+"F0.imprint","IMPRINT",FACE,{"disambiguationData":[TD([[makeQuery(id+"F0.imprint","IMPRINT",EDGE,{"derivedFrom":sQuery(id+"F0.wireOp",EDGE,"E49.bottom")}),-1.0]])]});
            var Q8;
            {var subQ0=sQuery(id+"F0.wireOp",EDGE,"E49.top");Q8=makeQuery(id+"F0.imprint","IMPRINT",FACE,{"disambiguationData":[TD([[makeQuery(id+"F0.imprint","IMPRINT",EDGE,{"derivedFrom":subQ0}),-1.0]])]});}
            var Q9;
            Q9=makeQuery(id+"F0.imprint","IMPRINT",FACE,{"disambiguationData":[TD([[makeQuery(id+"F0.imprint","IMPRINT",EDGE,{"derivedFrom":sQuery(id+"F0.wireOp",EDGE,"E13.right")}),1.0]])]});
            var Q10;
            {var subQ1=sQuery(id+"F0.wireOp",EDGE,"E61.top");Q10=makeQuery(id+"F0.imprint","IMPRINT",FACE,{"disambiguationData":[TD([[makeQuery(id+"F0.imprint","IMPRINT",EDGE,{"derivedFrom":subQ1}),-1.0]])]});}
            var Q11;
            Q11=makeQuery(id+"F0.imprint","IMPRINT",FACE,{"disambiguationData":[TD([[makeQuery(id+"F0.imprint","IMPRINT",EDGE,{"derivedFrom":sQuery(id+"F0.wireOp",EDGE,"E65.top")}),-1.0]])]});
            var Q12;
            Q12=makeQuery(id+"F0.imprint","IMPRINT",FACE,{"disambiguationData":[TD([[makeQuery(id+"F0.imprint","IMPRINT",EDGE,{"derivedFrom":sQuery(id+"F0.wireOp",EDGE,"E67.top")}),-1.0]])]});
            var Q13;
            {var subQ0=sQuery(id+"F0.wireOp",EDGE,"E76");Q13=makeQuery(id+"F0.imprint","IMPRINT",FACE,{"disambiguationData":[TD([[makeQuery(id+"F0.imprint","IMPRINT",EDGE,{"derivedFrom":subQ0}),1.0]])]});}
            var Q14;
            Q14=makeQuery(id+"F0.imprint","IMPRINT",FACE,{"disambiguationData":[TD([[makeQuery(id+"F0.imprint","IMPRINT",EDGE,{"derivedFrom":sQuery(id+"F0.wireOp",EDGE,"E70.top")}),-1.0]])]});
            var Q15;
            Q15=makeQuery(id+"F0.imprint","IMPRINT",FACE,{"disambiguationData":[TD([[makeQuery(id+"F0.imprint","IMPRINT",EDGE,{"derivedFrom":sQuery(id+"F0.wireOp",EDGE,"E72.top")}),-1.0]])]});
            var Q16;
            Q16=makeQuery(id+"F0.imprint","IMPRINT",FACE,{"disambiguationData":[TD([[makeQuery(id+"F0.imprint","IMPRINT",EDGE,{"derivedFrom":sQuery(id+"F0.wireOp",EDGE,"E74.top")}),-1.0]])]});
            var Q17;
            {var subQ0=sQuery(id+"F0.wireOp",EDGE,"E51.bottom");Q17=makeQuery(id+"F0.imprint","IMPRINT",FACE,{"disambiguationData":[TD([[makeQuery(id+"F0.imprint","IMPRINT",EDGE,{"derivedFrom":subQ0}),1.0]])]});}
            var Q18;
            Q18=makeQuery(id+"F0.imprint","IMPRINT",FACE,{"disambiguationData":[TD([[makeQuery(id+"F0.imprint","IMPRINT",EDGE,{"derivedFrom":sQuery(id+"F0.wireOp",EDGE,"E51.top")}),1.0]])]});
            var Q19;
            Q19=makeQuery(id+"F0.imprint","IMPRINT",FACE,{"disambiguationData":[TD([[makeQuery(id+"F0.imprint","IMPRINT",EDGE,{"derivedFrom":sQuery(id+"F0.wireOp",EDGE,"E56.bottom")}),-1.0]])]});
            var Q20;
            {var subQ3=sQuery(id+"F0.wireOp",EDGE,"E12.top");Q20=makeQuery(id+"F0.imprint","IMPRINT",FACE,{"disambiguationData":[TD([[makeQuery(id+"F0.imprint","IMPRINT",EDGE,{"derivedFrom":subQ3}),1.0]])]});}
            var Q21;
            Q21=makeQuery(id+"F0.imprint","IMPRINT",FACE,{"disambiguationData":[TD([[makeQuery(id+"F0.imprint","IMPRINT",EDGE,{"derivedFrom":sQuery(id+"F0.wireOp",EDGE,"E55.top")}),1.0]])]});
            var Q22;
            Q22=makeQuery(id+"F0.imprint","IMPRINT",FACE,{"disambiguationData":[TD([[makeQuery(id+"F0.imprint","IMPRINT",EDGE,{"derivedFrom":sQuery(id+"F0.wireOp",EDGE,"E52.bottom")}),1.0]])]});
            var Q23;
            {var subQ0=sQuery(id+"F0.wireOp",EDGE,"E53.bottom");Q23=makeQuery(id+"F0.imprint","IMPRINT",FACE,{"disambiguationData":[TD([[makeQuery(id+"F0.imprint","IMPRINT",EDGE,{"derivedFrom":subQ0}),-1.0]])]});}
            extrude(context, id + "F10", {"entities" : qUnion([Q0, Q1, Q2, Q3, Q4, Q5, Q6, Q7, Q8, Q9, Q10, Q11, Q12, Q13, Q14, Q15, Q16, Q17, Q18, Q19, Q20, Q21, Q22, Q23]), "oppositeDirection" : true, "depth" : 20 * mm, "offsetDistance" : 25 * mm});
        }
        {
            var Q0;
            Q0=makeQuery(id+"F0.imprint","IMPRINT",FACE,{"disambiguationData":[TD([[makeQuery(id+"F0.imprint","IMPRINT",EDGE,{"derivedFrom":sQuery(id+"F0.wireOp",EDGE,"E117.bottom")}),-1.0]])]});
            var Q1;
            {var subQ0=sQuery(id+"F0.wireOp",EDGE,"E123.right");var subQ1=sQuery(id+"F0.wireOp",EDGE,"E120");var subQ2=makeQuery(id+"F0.imprint","INTERSECT",VERTEX,{"derivedFrom":[subQ1,subQ0]});Q1=makeQuery(id+"F0.imprint","IMPRINT",FACE,{"disambiguationData":[TD([[makeQuery(id+"F0.imprint","IMPRINT",EDGE,{"disambiguationData":[TD([[subQ2,-1.0]])],"derivedFrom":subQ1}),-1.0]])]});}
            var Q2;
            Q2=makeQuery(id+"F0.imprint","IMPRINT",FACE,{"disambiguationData":[TD([[makeQuery(id+"F0.imprint","IMPRINT",EDGE,{"derivedFrom":sQuery(id+"F0.wireOp",EDGE,"E122")}),-1.0]])]});
            var Q3;
            {var subQ0=sQuery(id+"F0.wireOp",EDGE,"E123.right");var subQ1=sQuery(id+"F0.wireOp",EDGE,"E123.top");var subQ2=makeQuery(id+"F0.imprint","INTERSECT",VERTEX,{"derivedFrom":[subQ1,subQ0]});Q3=makeQuery(id+"F0.imprint","IMPRINT",FACE,{"disambiguationData":[TD([[makeQuery(id+"F0.imprint","IMPRINT",EDGE,{"disambiguationData":[TD([[subQ2,1.0]])],"derivedFrom":subQ1}),1.0]])]});}
            var Q4;
            Q4=makeQuery(id+"F0.imprint","IMPRINT",FACE,{"disambiguationData":[TD([[makeQuery(id+"F0.imprint","IMPRINT",EDGE,{"derivedFrom":sQuery(id+"F0.wireOp",EDGE,"E121")}),-1.0]])]});
            var Q5;
            {var subQ0=sQuery(id+"F0.wireOp",EDGE,"E81.right");var subQ1=sQuery(id+"F0.wireOp",EDGE,"E123.top");var subQ2=makeQuery(id+"F0.imprint","INTERSECT",VERTEX,{"derivedFrom":[subQ1,subQ0]});Q5=makeQuery(id+"F0.imprint","IMPRINT",FACE,{"disambiguationData":[TD([[makeQuery(id+"F0.imprint","IMPRINT",EDGE,{"disambiguationData":[TD([[subQ2,-1.0]])],"derivedFrom":subQ1}),1.0]])]});}
            var Q6;
            {var subQ0=sQuery(id+"F0.wireOp",EDGE,"E81.right");var subQ1=sQuery(id+"F0.wireOp",EDGE,"E120");var subQ2=makeQuery(id+"F0.imprint","INTERSECT",VERTEX,{"derivedFrom":[subQ1,subQ0]});Q6=makeQuery(id+"F0.imprint","IMPRINT",FACE,{"disambiguationData":[TD([[makeQuery(id+"F0.imprint","IMPRINT",EDGE,{"disambiguationData":[TD([[subQ2,1.0]])],"derivedFrom":subQ1}),-1.0]])]});}
            var Q7;
            Q7=makeQuery(id+"F0.imprint","IMPRINT",FACE,{"disambiguationData":[TD([[makeQuery(id+"F0.imprint","IMPRINT",EDGE,{"derivedFrom":sQuery(id+"F0.wireOp",EDGE,"E118.bottom")}),1.0]])]});
            extrude(context, id + "F11", {"entities" : qUnion([Q0, Q1, Q2, Q3, Q4, Q5, Q6, Q7]), "oppositeDirection" : true, "depth" : 2 * mm, "offsetDistance" : 25 * mm});
        }
        {
            var Q0;
            {var subQ10=sQuery(id+"F0.wireOp",EDGE,"E8.left");Q0=makeQuery(id+"F0.imprint","IMPRINT",FACE,{"disambiguationData":[TD([[makeQuery(id+"F0.imprint","IMPRINT",EDGE,{"derivedFrom":subQ10}),1.0]])]});}
            var Q1;
            {var subQ6=sQuery(id+"F0.wireOp",EDGE,"E12.top");Q1=makeQuery(id+"F0.imprint","IMPRINT",FACE,{"disambiguationData":[TD([[makeQuery(id+"F0.imprint","IMPRINT",EDGE,{"derivedFrom":subQ6}),-1.0]])]});}
            var Q2;
            {var subQ12=sQuery(id+"F0.wireOp",EDGE,"E80.left");var subQ17=makeQuery(id+"F0.imprint","IMPRINT",VERTEX,{"disambiguationData":[OD(0.0)],"derivedFrom":subQ12});Q2=makeQuery(id+"F0.imprint","IMPRINT",FACE,{"disambiguationData":[TD([[makeQuery(id+"F0.imprint","IMPRINT",EDGE,{"disambiguationData":[TD([[subQ17,-1.0]])],"derivedFrom":subQ12}),1.0]])]});}
            var Q3;
            {var subQ10=sQuery(id+"F0.wireOp",EDGE,"E118.bottom");Q3=makeQuery(id+"F0.imprint","IMPRINT",FACE,{"disambiguationData":[TD([[makeQuery(id+"F0.imprint","IMPRINT",EDGE,{"derivedFrom":subQ10}),-1.0]])]});}
            var Q4;
            Q4=makeQuery(id+"F0.imprint","IMPRINT",FACE,{"disambiguationData":[TD([[makeQuery(id+"F0.imprint","IMPRINT",EDGE,{"derivedFrom":sQuery(id+"F0.wireOp",EDGE,"E37.bottom")}),-1.0]])]});
            extrude(context, id + "F12", {"entities" : qUnion([Q0, Q1, Q2, Q3, Q4]), "oppositeDirection" : true, "depth" : 4 * mm, "offsetDistance" : 25 * mm});
        }
        {
            var Q0;
            {var subQ0=sQuery(id+"F0.wireOp",EDGE,"E113.right");Q0=makeQuery(id+"F0.imprint","IMPRINT",FACE,{"disambiguationData":[TD([[makeQuery(id+"F0.imprint","IMPRINT",EDGE,{"derivedFrom":subQ0}),-1.0]])]});}
            var Q1;
            {var subQ0=sQuery(id+"F0.wireOp",EDGE,"E37.right");Q1=makeQuery(id+"F0.imprint","IMPRINT",FACE,{"disambiguationData":[TD([[makeQuery(id+"F0.imprint","IMPRINT",EDGE,{"derivedFrom":subQ0}),1.0]])]});}
            var Q2;
            {var subQ3=sQuery(id+"F0.wireOp",EDGE,"E37.left");Q2=makeQuery(id+"F0.imprint","IMPRINT",FACE,{"disambiguationData":[TD([[makeQuery(id+"F0.imprint","IMPRINT",EDGE,{"derivedFrom":subQ3}),-1.0]])]});}
            extrude(context, id + "F13", {"entities" : qUnion([Q0, Q1, Q2]), "oppositeDirection" : true, "depth" : 4 * mm, "offsetDistance" : 25 * mm});
        }
        {
            var Q0;
            {var subQ3=sQuery(id+"F0.wireOp",EDGE,"E37.left");Q0=makeQuery(id+"F0.imprint","IMPRINT",FACE,{"disambiguationData":[TD([[makeQuery(id+"F0.imprint","IMPRINT",EDGE,{"derivedFrom":subQ3}),-1.0]])]});}
            extrude(context, id + "F14", {"entities" : qUnion([Q0]), "operationType" : NewBodyOperationType.REMOVE, "oppositeDirection" : true, "depth" : 2 * mm, "offsetDistance" : 25 * mm});
        }
        {
            var Q0;
            {var subQ0=sQuery(id+"F0.wireOp",EDGE,"E37.right");Q0=makeQuery(id+"F0.imprint","IMPRINT",FACE,{"disambiguationData":[TD([[makeQuery(id+"F0.imprint","IMPRINT",EDGE,{"derivedFrom":subQ0}),1.0]])]});}
            extrude(context, id + "F15", {"entities" : qUnion([Q0]), "operationType" : NewBodyOperationType.REMOVE, "oppositeDirection" : true, "depth" : 2 * mm, "offsetDistance" : 25 * mm});
        }
        {
            var Q0;
            Q0=makeQuery(id+"F0.imprint","IMPRINT",FACE,{"disambiguationData":[TD([[makeQuery(id+"F0.imprint","IMPRINT",EDGE,{"derivedFrom":sQuery(id+"F0.wireOp",EDGE,"E121")}),-1.0]])]});
            extrude(context, id + "F16", {"entities" : qUnion([Q0]), "operationType" : NewBodyOperationType.REMOVE, "oppositeDirection" : true, "depth" : .5 * mm, "offsetDistance" : 25 * mm});
        }
    });
